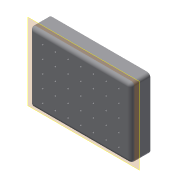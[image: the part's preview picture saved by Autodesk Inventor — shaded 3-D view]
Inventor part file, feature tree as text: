
AUTODESK INVENTOR PART (.ipt)
format: ipt  version: 2022 (Build 260153000, 153)  size: 249,856 bytes
history: native  units: mm
features: sketch x6, extrude x5, projected_geometry x4, other x3, plane x2, fillet x2, reference x2, hole x1, pattern_linear x1
ambient origin geometry x8: Origin, YZ Plane, XZ Plane, XY Plane, X Axis, Y Axis, Z Axis, Center Point
bodies: Solid1 (feature_tree)
feature tree (26):
  plane  "Work Plane1"
  extrude  "Extrusion1"  Depth=6.0mm TaperAngle=0.0deg
  sketch  "Sketch2"  dims[d5=10.0mm d6=0.0mm d8=8.0mm]
  plane  "Work Plane2"
  extrude  "Extrusion2"  Depth=8.0mm
  extrude  "Extrusion3"  Depth=6.0mm
  fillet  "Fillet1"  Radius=6.0mm
  fillet  "Fillet2"  Radius=120.0mm
  hole  "Hole1"  [1 undecoded]
  extrude  "Extrusion4"  Depth=70.0mm
  pattern_linear  "Rectangular Pattern1"  Count1=5  [1 undecoded]
  extrude  "Extrusion5"  Depth=8.0mm
  sketch  "Sketch1"  dims[d0=5.0mm d1=0.0mm d3=6.0mm d4=0.0mm]
  reference  "Reference1"
  projected_geometry  "Projected Loop1"
  sketch  "Sketch3"  dims[d9=0.0mm d10=6.0mm d11=6.0mm]
  projected_geometry  "Projected Loop2"
  projected_geometry  "Projected Loop3"
  sketch  "Sketch4"  dims[d12=2.9mm d13=6.0mm d14=6.0mm d15=4.0mm d16=90.0deg d17=15.0mm d18=20.594885mm d19=120.0mm]
  projected_geometry  "Projected Loop4"
  reference  "Reference2"
  sketch  "Sketch5"  dims[d20=80.0mm d21=2.9mm]
  sketch  "Sketch6"  dims[d22=10.0mm d23=0.0mm d24=70.0mm d26=20.0mm d27=50.0mm d29=20.0mm d30=8.0mm d31=8.0mm d32=7.0mm d33=0.0mm]
  other  "<userpath>\Documents\GitHub\cellstorm\INVENTOR\cellSTORM_v6.iam"
  other  "cellSTORM_v6.iam"
  other  "cellSTORM_Base_v0_R1:1"
note: 2 required parameter values undecoded (feature->parameter linkage not recoverable at this tier; creation-order binding heuristic only, values carry confidence <= 0.55)
